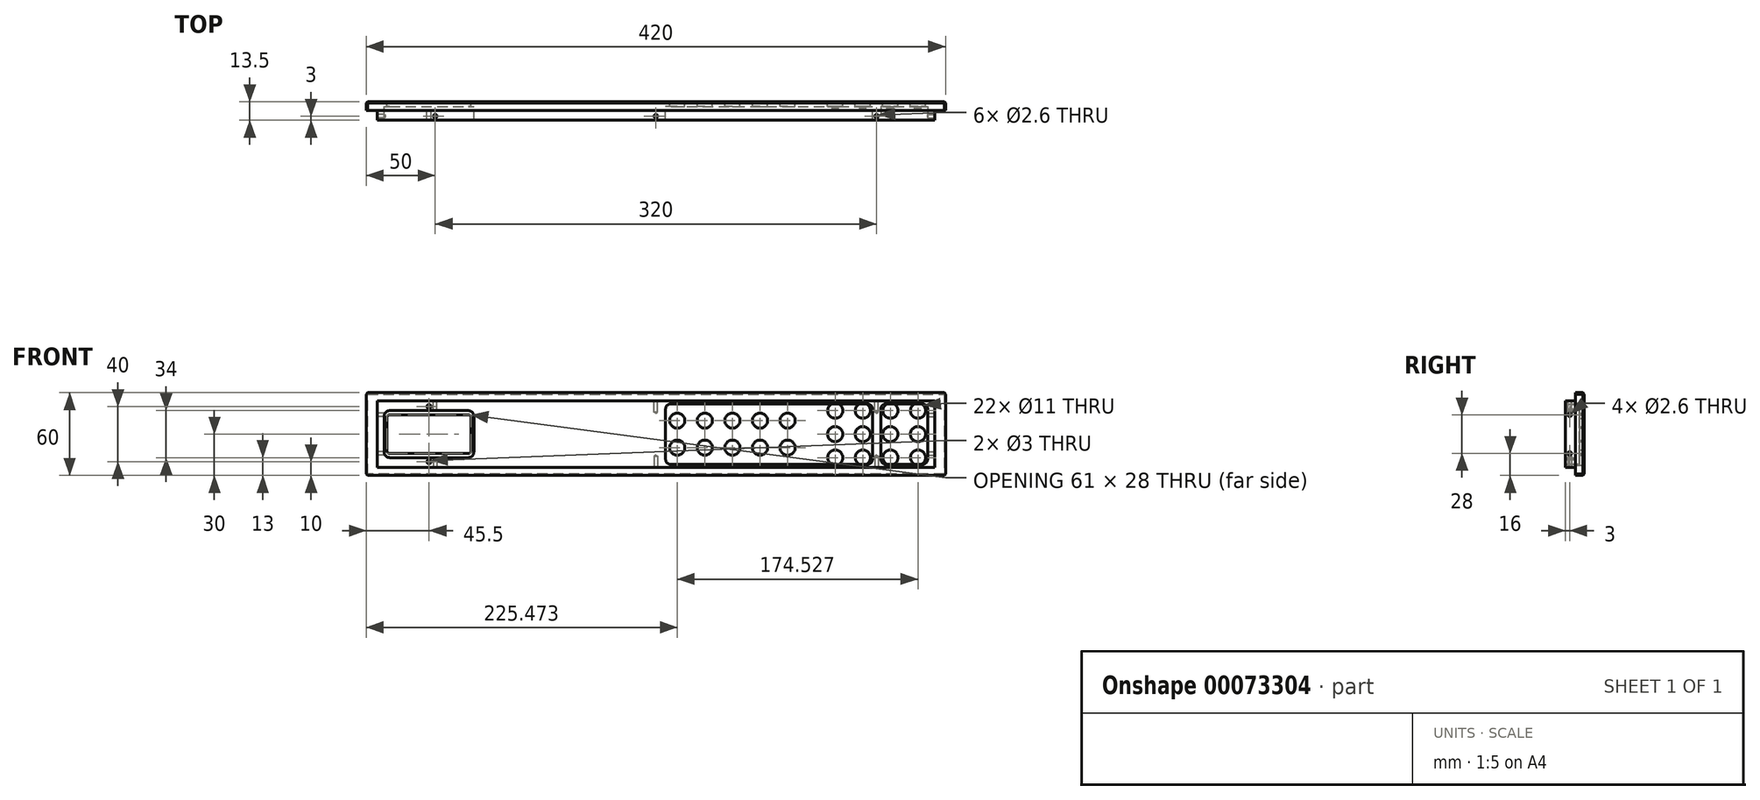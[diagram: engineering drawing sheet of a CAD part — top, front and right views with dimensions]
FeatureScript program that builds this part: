
annotation { "Feature Type Name" : "Feature", "Feature Type Description" : "" }
export const myFeature = defineFeature(function(context is Context, id is Id, definition is map)
    precondition{}
    {
        {
            var Q0;
            Q0=qCreatedBy(makeId("Right.planeOp"),FACE);
            var sketch = newSketch(context, id + "F0", { "sketchPlane" : qUnion([Q0])});
            skLineSegment(sketch, "E0.rect.bottom", {"start": v(-3.25, 30) * mm, "end": v(3.25, 30) * mm});
            skLineSegment(sketch, "E0.rect.top", {"start": v(-3.25, -30) * mm, "end": v(3.25, -30) * mm});
            skLineSegment(sketch, "E0.rect.left", {"start": v(-3.25, 30) * mm, "end": v(-3.25, -30) * mm});
            skLineSegment(sketch, "E0.rect.right", {"start": v(3.25, 30) * mm, "end": v(3.25, -30) * mm});
            skPoint(sketch, "E0.rect.middle", {"position": v(0, 0) * mm});
            skLineSegment(sketch, "E1", {"start": v(-3.25, 30) * mm, "end": v(-3.25, 24) * mm});
            skLineSegment(sketch, "E2", {"start": v(-3.25, 24) * mm, "end": v(-3.25, -24) * mm});
            skLineSegment(sketch, "E3", {"start": v(-3.25, 24) * mm, "end": v(-10.25, 24) * mm});
            skLineSegment(sketch, "E4.MirrorCS", {"start": v(-3.25, -24) * mm, "end": v(-10.25, -24) * mm});
            skLineSegment(sketch, "E5", {"start": v(-10.25, 24) * mm, "end": v(-10.25, -24) * mm});
            skSolve(sketch);
        }
        {
            var Q0;
            Q0=makeQuery(id+"F0.imprint","IMPRINT",FACE,{"disambiguationData":[TD([[makeQuery(id+"F0.imprint","IMPRINT",EDGE,{"derivedFrom":sQuery(id+"F0.wireOp",EDGE,"E0.rect.bottom")}),-1.0]])]});
            extrude(context, id + "F1", {"entities" : qUnion([Q0]), "endBound" : BoundingType.SYMMETRIC, "depth" : 420 * mm});
        }
        {
            var Q0;
            Q0 = qSketchRegion(id + "F0", true);
            extrude(context, id + "F2", {"entities" : qUnion([Q0]), "operationType" : NewBodyOperationType.ADD, "endBound" : BoundingType.SYMMETRIC, "depth" : 404 * mm});
        }
        {
            var Q0;
            Q0=makeQuery(id+"F2.opExtrude","SWEPT_FACE",FACE,{"disambiguationData":[OSD([sQuery(id+"F0.wireOp",EDGE,"E3")])]});
            var sketch = newSketch(context, id + "F3", { "sketchPlane" : qUnion([Q0])});
            skPoint(sketch, "E6", {"position": v(-160, -7.25) * mm});
            skPoint(sketch, "E7", {"position": v(0, -7.25) * mm});
            skPoint(sketch, "E8.MirrorP", {"position": v(160, -7.25) * mm});
            skSolve(sketch);
        }
        {
            var Q0;
            Q0=makeQuery(id+"F2.opExtrude","SWEPT_FACE",FACE,{"disambiguationData":[OSD([sQuery(id+"F0.wireOp",EDGE,"E4.MirrorCS")])]});
            var sketch = newSketch(context, id + "F4", { "sketchPlane" : qUnion([Q0])});
            skPoint(sketch, "E9", {"position": v(160, 7.25) * mm});
            skPoint(sketch, "E10.MirrorP", {"position": v(-160, 7.25) * mm});
            skPoint(sketch, "E11", {"position": v(0, 7.25) * mm});
            skSolve(sketch);
        }
        {
            var Q0;
            Q0=sQuery(id+"F3.wireOp",VERTEX,"6448b131-0878-4814-ae99-ac66ef3eb5f20.MirrorP");
            var Q1;
            Q1=sQuery(id+"F3.wireOp",VERTEX,"E7");
            var Q2;
            Q2=sQuery(id+"F3.wireOp",VERTEX,"E6");
            var Q3;
            Q3=sQuery(id+"F3.wireOp",VERTEX,"E8.MirrorP");
            var Q4;
            Q4=makeQuery(id+"F1.opExtrude","SWEPT_BODY",BODY,{"disambiguationData":[OSD([sQuery(id+"F0.wireOp",EDGE,"E0.rect.bottom"),sQuery(id+"F0.wireOp",EDGE,"E0.rect.top"),sQuery(id+"F0.wireOp",EDGE,"E0.rect.left"),sQuery(id+"F0.wireOp",EDGE,"E0.rect.right"),sQuery(id+"F0.wireOp",EDGE,"E1"),sQuery(id+"F0.wireOp",EDGE,"E2")])]});
            hole(context, id + "F5", {"style" : HoleStyle.SIMPLE, "holeDiameter" : 2.6 * mm, "endStyle" : HoleEndStyle.BLIND, "holeDepth" : 8 * mm, "locations" : qUnion([Q0, Q1, Q2, Q3]), "scope" : qUnion([Q4]), "tappedDepth" : 12 * mm, "tapClearance" : 3});
        }
        {
            var Q0;
            Q0=sQuery(id+"F4.wireOp",VERTEX,"E10.MirrorP");
            var Q1;
            Q1=sQuery(id+"F4.wireOp",VERTEX,"E11");
            var Q2;
            Q2=sQuery(id+"F4.wireOp",VERTEX,"E9");
            var Q3;
            Q3=makeQuery(id+"F1.opExtrude","SWEPT_BODY",BODY,{"disambiguationData":[OSD([sQuery(id+"F0.wireOp",EDGE,"E0.rect.bottom"),sQuery(id+"F0.wireOp",EDGE,"E0.rect.top"),sQuery(id+"F0.wireOp",EDGE,"E0.rect.left"),sQuery(id+"F0.wireOp",EDGE,"E0.rect.right"),sQuery(id+"F0.wireOp",EDGE,"E1"),sQuery(id+"F0.wireOp",EDGE,"E2")])]});
            hole(context, id + "F6", {"style" : HoleStyle.SIMPLE, "holeDiameter" : 2.6 * mm, "endStyle" : HoleEndStyle.BLIND, "holeDepth" : 8 * mm, "locations" : qUnion([Q0, Q1, Q2]), "scope" : qUnion([Q3]), "tappedDepth" : 12 * mm, "tapClearance" : 3});
        }
        {
            var Q0;
            Q0=makeQuery(id+"F2.opExtrude","CAP_FACE",FACE,{"disambiguationData":[OSD([sQuery(id+"F0.wireOp",EDGE,"E0.rect.bottom"),sQuery(id+"F0.wireOp",EDGE,"E0.rect.top"),sQuery(id+"F0.wireOp",EDGE,"E0.rect.left"),sQuery(id+"F0.wireOp",EDGE,"E0.rect.right"),sQuery(id+"F0.wireOp",EDGE,"E1"),sQuery(id+"F0.wireOp",EDGE,"E3"),sQuery(id+"F0.wireOp",EDGE,"E4.MirrorCS"),sQuery(id+"F0.wireOp",EDGE,"E5")])],"isStart":false});
            var sketch = newSketch(context, id + "F7", { "sketchPlane" : qUnion([Q0])});
            skPoint(sketch, "E12", {"position": v(-7.25, -14) * mm});
            skPoint(sketch, "E13.MirrorP", {"position": v(-7.25, 14) * mm});
            skSolve(sketch);
        }
        {
            var Q0;
            Q0=makeQuery(id+"F2.opExtrude","CAP_FACE",FACE,{"disambiguationData":[OSD([sQuery(id+"F0.wireOp",EDGE,"E0.rect.bottom"),sQuery(id+"F0.wireOp",EDGE,"E0.rect.top"),sQuery(id+"F0.wireOp",EDGE,"E0.rect.left"),sQuery(id+"F0.wireOp",EDGE,"E0.rect.right"),sQuery(id+"F0.wireOp",EDGE,"E1"),sQuery(id+"F0.wireOp",EDGE,"E3"),sQuery(id+"F0.wireOp",EDGE,"E4.MirrorCS"),sQuery(id+"F0.wireOp",EDGE,"E5")])],"isStart":true});
            var sketch = newSketch(context, id + "F8", { "sketchPlane" : qUnion([Q0])});
            skPoint(sketch, "E14", {"position": v(7.25, -14) * mm});
            skPoint(sketch, "E15.MirrorP", {"position": v(7.25, 14) * mm});
            skSolve(sketch);
        }
        {
            var Q0;
            Q0=sQuery(id+"F8.wireOp",VERTEX,"E14");
            var Q1;
            Q1=sQuery(id+"F8.wireOp",VERTEX,"E15.MirrorP");
            var Q2;
            Q2=makeQuery(id+"F1.opExtrude","SWEPT_BODY",BODY,{"disambiguationData":[OSD([sQuery(id+"F0.wireOp",EDGE,"E0.rect.bottom"),sQuery(id+"F0.wireOp",EDGE,"E0.rect.top"),sQuery(id+"F0.wireOp",EDGE,"E0.rect.left"),sQuery(id+"F0.wireOp",EDGE,"E0.rect.right"),sQuery(id+"F0.wireOp",EDGE,"E1"),sQuery(id+"F0.wireOp",EDGE,"E2")])]});
            hole(context, id + "F9", {"style" : HoleStyle.SIMPLE, "holeDiameter" : 2.6 * mm, "endStyle" : HoleEndStyle.BLIND, "holeDepth" : 6 * mm, "locations" : qUnion([Q0, Q1]), "scope" : qUnion([Q2]), "tappedDepth" : 12 * mm, "tapClearance" : 3});
        }
        {
            var Q0;
            Q0=sQuery(id+"F7.wireOp",VERTEX,"E12");
            var Q1;
            Q1=sQuery(id+"F7.wireOp",VERTEX,"E13.MirrorP");
            var Q2;
            Q2=makeQuery(id+"F1.opExtrude","SWEPT_BODY",BODY,{"disambiguationData":[OSD([sQuery(id+"F0.wireOp",EDGE,"E0.rect.bottom"),sQuery(id+"F0.wireOp",EDGE,"E0.rect.top"),sQuery(id+"F0.wireOp",EDGE,"E0.rect.left"),sQuery(id+"F0.wireOp",EDGE,"E0.rect.right"),sQuery(id+"F0.wireOp",EDGE,"E1"),sQuery(id+"F0.wireOp",EDGE,"E2")])]});
            hole(context, id + "F10", {"style" : HoleStyle.SIMPLE, "holeDiameter" : 2.6 * mm, "endStyle" : HoleEndStyle.BLIND, "holeDepth" : 15 * mm, "locations" : qUnion([Q0, Q1]), "scope" : qUnion([Q2])});
        }
        {
            var Q0;
            Q0=qCreatedBy(makeId("Front.planeOp"),FACE);
            var sketch = newSketch(context, id + "F11", { "sketchPlane" : qUnion([Q0])});
            skLineSegment(sketch, "E16.bottom", {"start": v(-195, 14) * mm, "end": v(-134, 14) * mm});
            skLineSegment(sketch, "E16.top", {"start": v(-195, -14) * mm, "end": v(-134, -14) * mm});
            skLineSegment(sketch, "E16.left", {"start": v(-195, 14) * mm, "end": v(-195, -14) * mm});
            skLineSegment(sketch, "E16.right", {"start": v(-134, 14) * mm, "end": v(-134, -14) * mm});
            skPoint(sketch, "E17", {"position": v(70, 10) * mm});
            skLineSegment(sketch, "E18", {"start": v(0, 0) * mm, "end": v(0, 52.08) * mm});
            skLineSegment(sketch, "E19", {"start": v(0, 52.08) * mm, "end": v(0, -56.97) * mm});
            skPoint(sketch, "E20.MirrorP", {"position": v(70, -10) * mm});
            skLineSegment(sketch, "E21", {"start": v(70, 10) * mm, "end": v(139.67, 10) * mm});
            skLineSegment(sketch, "E22", {"start": v(70, -10) * mm, "end": v(130, -10) * mm});
            skPoint(sketch, "E23", {"position": v(100, 10) * mm});
            skPoint(sketch, "E23.positionSnap0", {"position": v(100, -10) * mm});
            skPoint(sketch, "E24", {"position": v(130, 10) * mm});
            skPoint(sketch, "E25.MirrorP", {"position": v(130, -10) * mm});
            skLineSegment(sketch, "E26", {"start": v(70, 10) * mm, "end": v(-24.67, 10) * mm});
            skLineSegment(sketch, "E27", {"start": v(70, -10) * mm, "end": v(-27.1, -10) * mm});
            skPoint(sketch, "E28", {"position": v(40, 10) * mm});
            skPoint(sketch, "E29", {"position": v(10, 10) * mm});
            skPoint(sketch, "E30.MirrorP", {"position": v(40, -10) * mm});
            skPoint(sketch, "E31.MirrorP", {"position": v(10, -10) * mm});
            skLineSegment(sketch, "E32.bottom", {"start": v(200, 24) * mm, "end": v(-13.01, 24) * mm});
            skLineSegment(sketch, "E32.top", {"start": v(200, -24) * mm, "end": v(-13.01, -24) * mm});
            skLineSegment(sketch, "E32.left", {"start": v(200, 24) * mm, "end": v(200, -24) * mm});
            skLineSegment(sketch, "E32.right", {"start": v(-13.01, 24) * mm, "end": v(-13.01, -24) * mm});
            skLineSegment(sketch, "E33.bottom", {"start": v(-199.88, -17.24) * mm, "end": v(-129.22, -17.24) * mm});
            skLineSegment(sketch, "E33.top", {"start": v(-199.88, 17.31) * mm, "end": v(-129.22, 17.31) * mm});
            skLineSegment(sketch, "E33.left", {"start": v(-199.88, -17.24) * mm, "end": v(-199.88, 17.31) * mm});
            skLineSegment(sketch, "E33.right", {"start": v(-129.22, -17.24) * mm, "end": v(-129.22, 17.31) * mm});
            skLineSegment(sketch, "E34.bottom", {"start": v(-97.81, -13.33) * mm, "end": v(-69.7, -13.33) * mm});
            skLineSegment(sketch, "E34.top", {"start": v(-97.81, 5.05) * mm, "end": v(-69.7, 5.05) * mm});
            skLineSegment(sketch, "E34.left", {"start": v(-97.81, -13.33) * mm, "end": v(-97.81, 5.05) * mm});
            skLineSegment(sketch, "E34.right", {"start": v(-69.7, -13.33) * mm, "end": v(-69.7, 5.05) * mm});
            skSolve(sketch);
        }
        {
            var Q0;
            Q0=makeQuery(id+"F11.imprint","IMPRINT",FACE,{"disambiguationData":[TD([[makeQuery(id+"F11.imprint","IMPRINT",EDGE,{"derivedFrom":sQuery(id+"F11.wireOp",EDGE,"E16.bottom")}),-1.0]])]});
            extrude(context, id + "F12", {"entities" : qUnion([Q0]), "endBound" : BoundingType.SYMMETRIC, "depth" : 25 * mm});
        }
        {
            var Q0;
            Q0=makeQuery(id+"F12.opExtrude","SWEPT_BODY",BODY,{"disambiguationData":[OSD([sQuery(id+"F11.wireOp",EDGE,"E16.bottom"),sQuery(id+"F11.wireOp",EDGE,"E16.top"),sQuery(id+"F11.wireOp",EDGE,"E16.left"),sQuery(id+"F11.wireOp",EDGE,"E16.right")])]});
            var Q1;
            Q1=makeQuery(id+"F1.opExtrude","SWEPT_BODY",BODY,{"disambiguationData":[OSD([sQuery(id+"F0.wireOp",EDGE,"E0.rect.bottom"),sQuery(id+"F0.wireOp",EDGE,"E0.rect.top"),sQuery(id+"F0.wireOp",EDGE,"E0.rect.left"),sQuery(id+"F0.wireOp",EDGE,"E0.rect.right"),sQuery(id+"F0.wireOp",EDGE,"E1"),sQuery(id+"F0.wireOp",EDGE,"E2")])]});
            booleanBodies(context, id + "F13", {"operationType" : BooleanOperationType.SUBTRACTION, "tools" : qUnion([Q0]), "targets" : qUnion([Q1])});
        }
        {
            var Q0;
            Q0=makeQuery(id+"F1.opExtrude","SWEPT_FACE",FACE,{"disambiguationData":[OSD([sQuery(id+"F0.wireOp",EDGE,"E0.rect.right")])]});
            var sketch = newSketch(context, id + "F14", { "sketchPlane" : qUnion([Q0])});
            skLineSegment(sketch, "E35.bottom", {"start": v(131, 15.5) * mm, "end": v(198, 15.5) * mm});
            skLineSegment(sketch, "E35.top", {"start": v(131, -15.5) * mm, "end": v(198, -15.5) * mm});
            skLineSegment(sketch, "E35.left", {"start": v(131, 15.5) * mm, "end": v(131, -15.5) * mm});
            skLineSegment(sketch, "E35.right", {"start": v(198, 15.5) * mm, "end": v(198, -15.5) * mm});
            skLineSegment(sketch, "E36", {"start": v(164.5, 15.5) * mm, "end": v(164.5, 25.5) * mm});
            skLineSegment(sketch, "E37", {"start": v(164.5, -15.5) * mm, "end": v(164.5, -25.5) * mm});
            skLineSegment(sketch, "E38", {"start": v(131, -15.5) * mm, "end": v(164.5, -25.5) * mm});
            skLineSegment(sketch, "E39", {"start": v(164.5, -25.5) * mm, "end": v(198, -15.5) * mm});
            skLineSegment(sketch, "E40", {"start": v(131, 15.5) * mm, "end": v(164.5, 25.5) * mm});
            skLineSegment(sketch, "E41", {"start": v(164.5, 25.5) * mm, "end": v(198, 15.5) * mm});
            skPoint(sketch, "E42", {"position": v(164.5, -20) * mm});
            skPoint(sketch, "E43", {"position": v(164.5, 20) * mm});
            skSolve(sketch);
        }
        {
            var Q0;
            Q0=sQuery(id+"F14.wireOp",VERTEX,"E43");
            var Q1;
            Q1=sQuery(id+"F14.wireOp",VERTEX,"E42");
            var Q2;
            Q2=makeQuery(id+"F1.opExtrude","SWEPT_BODY",BODY,{"disambiguationData":[OSD([sQuery(id+"F0.wireOp",EDGE,"E0.rect.bottom"),sQuery(id+"F0.wireOp",EDGE,"E0.rect.top"),sQuery(id+"F0.wireOp",EDGE,"E0.rect.left"),sQuery(id+"F0.wireOp",EDGE,"E0.rect.right"),sQuery(id+"F0.wireOp",EDGE,"E1"),sQuery(id+"F0.wireOp",EDGE,"E2")])]});
            hole(context, id + "F15", {"style" : HoleStyle.SIMPLE, "holeDiameter" : 3 * mm, "endStyle" : HoleEndStyle.THROUGH, "locations" : qUnion([Q0, Q1]), "scope" : qUnion([Q2]), "isTappedThrough" : true});
        }
        {
            var Q0;
            Q0=makeQuery(id+"F1.opExtrude","SWEPT_FACE",FACE,{"disambiguationData":[OSD([sQuery(id+"F0.wireOp",EDGE,"E0.rect.right")])]});
            var sketch = newSketch(context, id + "F16", { "sketchPlane" : qUnion([Q0])});
            skPoint(sketch, "E44", {"position": v(-190, 0) * mm});
            skPoint(sketch, "E45", {"position": v(-170, 0) * mm});
            skPoint(sketch, "E46", {"position": v(-95.47, -9.8) * mm});
            skPoint(sketch, "E47", {"position": v(-190, 17) * mm});
            skPoint(sketch, "E48", {"position": v(-170, 17) * mm});
            skLineSegment(sketch, "E49", {"start": v(0, 0) * mm, "end": v(0, 23.5) * mm});
            skLineSegment(sketch, "E50", {"start": v(0, 23.5) * mm, "end": v(0, -27.54) * mm});
            skPoint(sketch, "E50.endSnap0", {"position": v(0, -29) * mm});
            skPoint(sketch, "E51.MirrorP", {"position": v(15, 10) * mm});
            skPoint(sketch, "E52.MirrorP", {"position": v(15, -10) * mm});
            skPoint(sketch, "E53.MirrorP", {"position": v(-95.47, 9.8) * mm});
            skLineSegment(sketch, "E54", {"start": v(-115.47, -9.36) * mm, "end": v(-115.47, 29) * mm});
            skLineSegment(sketch, "E55", {"start": v(-95.47, 9.8) * mm, "end": v(-35.47, 9.8) * mm});
            skPoint(sketch, "E56", {"position": v(-75.47, 9.8) * mm});
            skPoint(sketch, "E57", {"position": v(-55.47, 9.8) * mm});
            skPoint(sketch, "E58.MirrorP", {"position": v(-75.47, -9.8) * mm});
            skPoint(sketch, "E59.MirrorP", {"position": v(-55.47, -9.8) * mm});
            skLineSegment(sketch, "E60", {"start": v(0, 0) * mm, "end": v(-215.2, 0) * mm});
            skPoint(sketch, "E61.MirrorP", {"position": v(-170, -17) * mm});
            skPoint(sketch, "E62.MirrorP", {"position": v(-190, -17) * mm});
            skPoint(sketch, "E63", {"position": v(-35.47, 9.8) * mm});
            skLineSegment(sketch, "E64", {"start": v(-35.47, 9.8) * mm, "end": v(-3.53, 9.8) * mm});
            skPoint(sketch, "E65", {"position": v(-15.47, 9.8) * mm});
            skPoint(sketch, "E66.MirrorP", {"position": v(-35.47, -9.8) * mm});
            skPoint(sketch, "E67.MirrorP", {"position": v(-15.47, -9.8) * mm});
            skLineSegment(sketch, "E68", {"start": v(-170, 0) * mm, "end": v(-160, 0) * mm});
            skLineSegment(sketch, "E69", {"start": v(-160, 0) * mm, "end": v(-160, 63.24) * mm});
            skLineSegment(sketch, "E70", {"start": v(-160, 63.24) * mm, "end": v(-160, -51.93) * mm});
            skPoint(sketch, "E71.MirrorP", {"position": v(-150, 17) * mm});
            skPoint(sketch, "E72.MirrorP", {"position": v(-130, 17) * mm});
            skPoint(sketch, "E73.MirrorP", {"position": v(-150, 0) * mm});
            skPoint(sketch, "E74.MirrorP", {"position": v(-130, 0) * mm});
            skPoint(sketch, "E75.MirrorP", {"position": v(-150, -17) * mm});
            skPoint(sketch, "E76.MirrorP", {"position": v(-130, -17) * mm});
            skSolve(sketch);
        }
        {
            var Q0;
            Q0=sQuery(id+"F16.wireOp",VERTEX,"E47");
            var Q1;
            Q1=sQuery(id+"F16.wireOp",VERTEX,"E48");
            var Q2;
            Q2=sQuery(id+"F16.wireOp",VERTEX,"E45");
            var Q3;
            Q3=sQuery(id+"F16.wireOp",VERTEX,"E44");
            var Q4;
            Q4=sQuery(id+"F16.wireOp",VERTEX,"04784362-13c3-4ef5-a573-1091d004b7ea0.MirrorP");
            var Q5;
            Q5=sQuery(id+"F16.wireOp",VERTEX,"63e7e146-2827-4e0b-9712-db2128c02bd60.MirrorP");
            var Q6;
            Q6=sQuery(id+"F16.wireOp",VERTEX,"E56");
            var Q7;
            Q7=sQuery(id+"F16.wireOp",VERTEX,"E57");
            var Q8;
            Q8=sQuery(id+"F16.wireOp",VERTEX,"E58.MirrorP");
            var Q9;
            Q9=sQuery(id+"F16.wireOp",VERTEX,"E59.MirrorP");
            var Q10;
            Q10=sQuery(id+"F16.wireOp",VERTEX,"E61.MirrorP");
            var Q11;
            Q11=sQuery(id+"F16.wireOp",VERTEX,"E62.MirrorP");
            var Q12;
            Q12=sQuery(id+"F16.wireOp",VERTEX,"E63");
            var Q13;
            Q13=sQuery(id+"F16.wireOp",VERTEX,"E65");
            var Q14;
            Q14=sQuery(id+"F16.wireOp",VERTEX,"E67.MirrorP");
            var Q15;
            Q15=sQuery(id+"F16.wireOp",VERTEX,"E66.MirrorP");
            var Q16;
            Q16=sQuery(id+"F16.wireOp",VERTEX,"E71.MirrorP");
            var Q17;
            Q17=sQuery(id+"F16.wireOp",VERTEX,"E72.MirrorP");
            var Q18;
            Q18=sQuery(id+"F16.wireOp",VERTEX,"E74.MirrorP");
            var Q19;
            Q19=sQuery(id+"F16.wireOp",VERTEX,"E73.MirrorP");
            var Q20;
            Q20=sQuery(id+"F16.wireOp",VERTEX,"E75.MirrorP");
            var Q21;
            Q21=sQuery(id+"F16.wireOp",VERTEX,"E76.MirrorP");
            var Q22;
            Q22=makeQuery(id+"F1.opExtrude","SWEPT_BODY",BODY,{"disambiguationData":[OSD([sQuery(id+"F0.wireOp",EDGE,"E0.rect.bottom"),sQuery(id+"F0.wireOp",EDGE,"E0.rect.top"),sQuery(id+"F0.wireOp",EDGE,"E0.rect.left"),sQuery(id+"F0.wireOp",EDGE,"E0.rect.right"),sQuery(id+"F0.wireOp",EDGE,"E1"),sQuery(id+"F0.wireOp",EDGE,"E2")])]});
            hole(context, id + "F17", {"style" : HoleStyle.SIMPLE, "endStyle" : HoleEndStyle.BLIND, "holeDiameter" : 11 * mm, "holeDepth" : 5 * mm, "locations" : qUnion([Q0, Q1, Q2, Q3, Q4, Q5, Q6, Q7, Q8, Q9, Q10, Q11, Q12, Q13, Q14, Q15, Q16, Q17, Q18, Q19, Q20, Q21]), "scope" : qUnion([Q22]), "tappedDepth" : 12 * mm, "tapClearance" : 3});
        }
        {
            var Q0;
            Q0=sQuery(id+"F16.wireOp",VERTEX,"f41b2cb0-a797-4a80-b0a8-9d696aceb2f3");
            var Q1;
            Q1=sQuery(id+"F16.wireOp",VERTEX,"782acfd5-4f50-4505-aa6c-89699b7f583a");
            var Q2;
            Q2=sQuery(id+"F16.wireOp",VERTEX,"E46");
            var Q3;
            Q3=sQuery(id+"F16.wireOp",VERTEX,"496bf54d-163d-4c96-88b8-d3f3045ecf5c");
            var Q4;
            Q4=sQuery(id+"F16.wireOp",VERTEX,"E53.MirrorP");
            var Q5;
            Q5=sQuery(id+"F16.wireOp",VERTEX,"17ab3d33-8b4b-4c6c-ad7c-a89e3acb6b3c0.MirrorP");
            var Q6;
            Q6=sQuery(id+"F16.wireOp",VERTEX,"a3c92349-ed62-4d63-99aa-c9f1a0d295a10.MirrorP");
            var Q7;
            Q7=sQuery(id+"F16.wireOp",VERTEX,"ef22c00b-a273-4283-a508-ab80f66826260.MirrorP");
            var Q8;
            Q8=makeQuery(id+"F1.opExtrude","SWEPT_BODY",BODY,{"disambiguationData":[OSD([sQuery(id+"F0.wireOp",EDGE,"E0.rect.bottom"),sQuery(id+"F0.wireOp",EDGE,"E0.rect.top"),sQuery(id+"F0.wireOp",EDGE,"E0.rect.left"),sQuery(id+"F0.wireOp",EDGE,"E0.rect.right"),sQuery(id+"F0.wireOp",EDGE,"E1"),sQuery(id+"F0.wireOp",EDGE,"E2")])]});
            hole(context, id + "F18", {"style" : HoleStyle.SIMPLE, "endStyle" : HoleEndStyle.BLIND, "holeDiameter" : 11 * mm, "holeDepth" : 5 * mm, "locations" : qUnion([Q0, Q1, Q2, Q3, Q4, Q5, Q6, Q7]), "scope" : qUnion([Q8]), "tappedDepth" : 12 * mm, "tapClearance" : 3});
        }
        {
            var Q0;
            Q0=makeQuery(id+"F1.opExtrude","CAP_EDGE",EDGE,{"disambiguationData":[OSD([sQuery(id+"F0.wireOp",EDGE,"E0.rect.bottom")])],"isStart":false});
            var Q1;
            Q1=makeQuery(id+"F1.opExtrude","SWEPT_EDGE",EDGE,{"disambiguationData":[OSD([sQuery(id+"F0.wireOp",EDGE,"E0.rect.bottom"),sQuery(id+"F0.wireOp",EDGE,"E0.rect.right")])]});
            var Q2;
            Q2=makeQuery(id+"F1.opExtrude","CAP_EDGE",EDGE,{"disambiguationData":[OSD([sQuery(id+"F0.wireOp",EDGE,"E0.rect.right")])],"isStart":false});
            var Q3;
            Q3=makeQuery(id+"F1.opExtrude","SWEPT_EDGE",EDGE,{"disambiguationData":[OSD([sQuery(id+"F0.wireOp",EDGE,"E0.rect.top"),sQuery(id+"F0.wireOp",EDGE,"E0.rect.right")])]});
            var Q4;
            Q4=makeQuery(id+"F1.opExtrude","CAP_EDGE",EDGE,{"disambiguationData":[OSD([sQuery(id+"F0.wireOp",EDGE,"E0.rect.right")])],"isStart":true});
            var Q5;
            Q5=makeQuery(id+"F1.opExtrude","CAP_EDGE",EDGE,{"disambiguationData":[OSD([sQuery(id+"F0.wireOp",EDGE,"E0.rect.bottom")])],"isStart":true});
            var Q6;
            Q6=makeQuery(id+"F1.opExtrude","CAP_EDGE",EDGE,{"disambiguationData":[OSD([sQuery(id+"F0.wireOp",EDGE,"E0.rect.top")])],"isStart":true});
            var Q7;
            Q7=makeQuery(id+"F1.opExtrude","CAP_EDGE",EDGE,{"disambiguationData":[OSD([sQuery(id+"F0.wireOp",EDGE,"E0.rect.top")])],"isStart":false});
            chamfer(context, id + "F19", {"entities" : qUnion([Q0, Q1, Q2, Q3, Q4, Q5, Q6, Q7]), "width" : 1 * mm, "tangentPropagation" : true});
        }
        {
            var Q0;
            Q0=makeQuery(id+"F2.opExtrude","SWEPT_FACE",FACE,{"disambiguationData":[OSD([sQuery(id+"F0.wireOp",EDGE,"E5")])]});
            var sketch = newSketch(context, id + "F20", { "sketchPlane" : qUnion([Q0])});
            skLineSegment(sketch, "E77.bottom", {"start": v(7, 22) * mm, "end": v(157, 22) * mm});
            skLineSegment(sketch, "E77.top", {"start": v(7, -22) * mm, "end": v(157, -22) * mm});
            skLineSegment(sketch, "E77.left", {"start": v(7, 22) * mm, "end": v(7, -22) * mm});
            skLineSegment(sketch, "E77.right", {"start": v(157, 22) * mm, "end": v(157, -22) * mm});
            skLineSegment(sketch, "E78.bottom", {"start": v(-197, 17) * mm, "end": v(-132, 17) * mm});
            skLineSegment(sketch, "E78.top", {"start": v(-197, -17) * mm, "end": v(-132, -17) * mm});
            skLineSegment(sketch, "E78.left", {"start": v(-197, 17) * mm, "end": v(-197, -17) * mm});
            skLineSegment(sketch, "E78.right", {"start": v(-132, 17) * mm, "end": v(-132, -17) * mm});
            skLineSegment(sketch, "E79.bottom", {"start": v(-108.25, 10.64) * mm, "end": v(-62, 10.64) * mm});
            skLineSegment(sketch, "E79.top", {"start": v(-108.25, -10.76) * mm, "end": v(-62, -10.76) * mm});
            skLineSegment(sketch, "E79.left", {"start": v(-108.25, 10.64) * mm, "end": v(-108.25, -10.76) * mm});
            skLineSegment(sketch, "E79.right", {"start": v(-62, 10.64) * mm, "end": v(-62, -10.76) * mm});
            skLineSegment(sketch, "E80.bottom", {"start": v(163, -21.98) * mm, "end": v(197, -21.98) * mm});
            skLineSegment(sketch, "E80.top", {"start": v(163, 22) * mm, "end": v(197, 22) * mm});
            skLineSegment(sketch, "E80.left", {"start": v(163, -21.98) * mm, "end": v(163, 22) * mm});
            skLineSegment(sketch, "E80.right", {"start": v(197, -21.98) * mm, "end": v(197, 22) * mm});
            skSolve(sketch);
        }
        {
            var Q0;
            Q0=makeQuery(id+"F20.imprint","IMPRINT",FACE,{"disambiguationData":[TD([[makeQuery(id+"F20.imprint","IMPRINT",EDGE,{"derivedFrom":sQuery(id+"F20.wireOp",EDGE,"E78.bottom")}),-1.0]])]});
            extrude(context, id + "F21", {"entities" : qUnion([Q0]), "operationType" : NewBodyOperationType.REMOVE, "endBound" : BoundingType.SYMMETRIC, "depth" : 20 * mm});
        }
        {
            var Q0;
            Q0=makeQuery(id+"F13.opBoolean","COPY",EDGE,{"derivedFrom":makeQuery(id+"F12.opExtrude","SWEPT_EDGE",EDGE,{"disambiguationData":[OSD([sQuery(id+"F11.wireOp",EDGE,"E16.bottom"),sQuery(id+"F11.wireOp",EDGE,"E16.left")])]})});
            var Q1;
            Q1=makeQuery(id+"F13.opBoolean","COPY",EDGE,{"derivedFrom":makeQuery(id+"F12.opExtrude","SWEPT_EDGE",EDGE,{"disambiguationData":[OSD([sQuery(id+"F11.wireOp",EDGE,"E16.bottom"),sQuery(id+"F11.wireOp",EDGE,"E16.right")])]})});
            var Q2;
            Q2=makeQuery(id+"F13.opBoolean","COPY",EDGE,{"derivedFrom":makeQuery(id+"F12.opExtrude","SWEPT_EDGE",EDGE,{"disambiguationData":[OSD([sQuery(id+"F11.wireOp",EDGE,"E16.top"),sQuery(id+"F11.wireOp",EDGE,"E16.left")])]})});
            var Q3;
            Q3=makeQuery(id+"F13.opBoolean","COPY",EDGE,{"derivedFrom":makeQuery(id+"F12.opExtrude","SWEPT_EDGE",EDGE,{"disambiguationData":[OSD([sQuery(id+"F11.wireOp",EDGE,"E16.top"),sQuery(id+"F11.wireOp",EDGE,"E16.right")])]})});
            fillet(context, id + "F22", {"entities" : qUnion([Q0, Q1, Q2, Q3]), "radius" : 2 * mm, "tangentPropagation" : true, "allowEdgeOverflow" : false});
        }
        {
            var Q0;
            Q0=makeQuery(id+"F21.boolean.opBoolean","COPY",EDGE,{"derivedFrom":makeQuery(id+"F21.opExtrude","SWEPT_EDGE",EDGE,{"disambiguationData":[OSD([sQuery(id+"F20.wireOp",EDGE,"E78.bottom"),sQuery(id+"F20.wireOp",EDGE,"E78.left")])]})});
            var Q1;
            Q1=makeQuery(id+"F21.boolean.opBoolean","COPY",EDGE,{"derivedFrom":makeQuery(id+"F21.opExtrude","SWEPT_EDGE",EDGE,{"disambiguationData":[OSD([sQuery(id+"F20.wireOp",EDGE,"E78.bottom"),sQuery(id+"F20.wireOp",EDGE,"E78.right")])]})});
            var Q2;
            Q2=makeQuery(id+"F21.boolean.opBoolean","COPY",EDGE,{"derivedFrom":makeQuery(id+"F21.opExtrude","SWEPT_EDGE",EDGE,{"disambiguationData":[OSD([sQuery(id+"F20.wireOp",EDGE,"E78.top"),sQuery(id+"F20.wireOp",EDGE,"E78.right")])]})});
            var Q3;
            Q3=makeQuery(id+"F21.boolean.opBoolean","COPY",EDGE,{"derivedFrom":makeQuery(id+"F21.opExtrude","SWEPT_EDGE",EDGE,{"disambiguationData":[OSD([sQuery(id+"F20.wireOp",EDGE,"E78.top"),sQuery(id+"F20.wireOp",EDGE,"E78.left")])]})});
            fillet(context, id + "F23", {"entities" : qUnion([Q0, Q1, Q2, Q3]), "radius" : 4 * mm, "tangentPropagation" : true, "allowEdgeOverflow" : false});
        }
        {
            var Q0;
            Q0=makeQuery(id+"F20.imprint","IMPRINT",FACE,{"disambiguationData":[TD([[makeQuery(id+"F20.imprint","IMPRINT",EDGE,{"derivedFrom":sQuery(id+"F20.wireOp",EDGE,"E77.bottom")}),-1.0]])]});
            extrude(context, id + "F24", {"entities" : qUnion([Q0]), "operationType" : NewBodyOperationType.REMOVE, "endBound" : BoundingType.SYMMETRIC, "depth" : 20 * mm});
        }
        {
            var Q0;
            Q0=makeQuery(id+"F24.boolean.opBoolean","COPY",EDGE,{"derivedFrom":makeQuery(id+"F24.opExtrude","SWEPT_EDGE",EDGE,{"disambiguationData":[OSD([sQuery(id+"F20.wireOp",EDGE,"E77.bottom"),sQuery(id+"F20.wireOp",EDGE,"E77.right")])]})});
            var Q1;
            Q1=makeQuery(id+"F24.boolean.opBoolean","COPY",EDGE,{"derivedFrom":makeQuery(id+"F24.opExtrude","SWEPT_EDGE",EDGE,{"disambiguationData":[OSD([sQuery(id+"F20.wireOp",EDGE,"E77.top"),sQuery(id+"F20.wireOp",EDGE,"E77.right")])]})});
            var Q2;
            Q2=makeQuery(id+"F24.boolean.opBoolean","COPY",EDGE,{"derivedFrom":makeQuery(id+"F24.opExtrude","SWEPT_EDGE",EDGE,{"disambiguationData":[OSD([sQuery(id+"F20.wireOp",EDGE,"E77.top"),sQuery(id+"F20.wireOp",EDGE,"E77.left")])]})});
            var Q3;
            Q3=makeQuery(id+"F24.boolean.opBoolean","COPY",EDGE,{"derivedFrom":makeQuery(id+"F24.opExtrude","SWEPT_EDGE",EDGE,{"disambiguationData":[OSD([sQuery(id+"F20.wireOp",EDGE,"E77.bottom"),sQuery(id+"F20.wireOp",EDGE,"E77.left")])]})});
            fillet(context, id + "F25", {"entities" : qUnion([Q0, Q1, Q2, Q3]), "radius" : 4 * mm, "tangentPropagation" : true, "allowEdgeOverflow" : false});
        }
        {
            var Q0;
            Q0=makeQuery(id+"F20.imprint","IMPRINT",FACE,{"disambiguationData":[TD([[makeQuery(id+"F20.imprint","IMPRINT",EDGE,{"derivedFrom":sQuery(id+"F20.wireOp",EDGE,"E80.bottom")}),1.0]])]});
            extrude(context, id + "F26", {"entities" : qUnion([Q0]), "operationType" : NewBodyOperationType.REMOVE, "endBound" : BoundingType.SYMMETRIC, "oppositeDirection" : true, "depth" : 20 * mm});
        }
        {
            var Q0;
            Q0=makeQuery(id+"F26.boolean.opBoolean","COPY",EDGE,{"derivedFrom":makeQuery(id+"F26.opExtrude","SWEPT_EDGE",EDGE,{"disambiguationData":[OSD([sQuery(id+"F20.wireOp",EDGE,"E80.bottom"),sQuery(id+"F20.wireOp",EDGE,"E80.left")])]})});
            var Q1;
            Q1=makeQuery(id+"F26.boolean.opBoolean","COPY",EDGE,{"derivedFrom":makeQuery(id+"F26.opExtrude","SWEPT_EDGE",EDGE,{"disambiguationData":[OSD([sQuery(id+"F20.wireOp",EDGE,"E80.top"),sQuery(id+"F20.wireOp",EDGE,"E80.left")])]})});
            var Q2;
            Q2=makeQuery(id+"F26.boolean.opBoolean","COPY",EDGE,{"derivedFrom":makeQuery(id+"F26.opExtrude","SWEPT_EDGE",EDGE,{"disambiguationData":[OSD([sQuery(id+"F20.wireOp",EDGE,"E80.top"),sQuery(id+"F20.wireOp",EDGE,"E80.right")])]})});
            var Q3;
            Q3=makeQuery(id+"F26.boolean.opBoolean","COPY",EDGE,{"derivedFrom":makeQuery(id+"F26.opExtrude","SWEPT_EDGE",EDGE,{"disambiguationData":[OSD([sQuery(id+"F20.wireOp",EDGE,"E80.bottom"),sQuery(id+"F20.wireOp",EDGE,"E80.right")])]})});
            fillet(context, id + "F27", {"entities" : qUnion([Q0, Q1, Q2, Q3]), "radius" : 4 * mm, "tangentPropagation" : true, "allowEdgeOverflow" : false});
        }
    });
